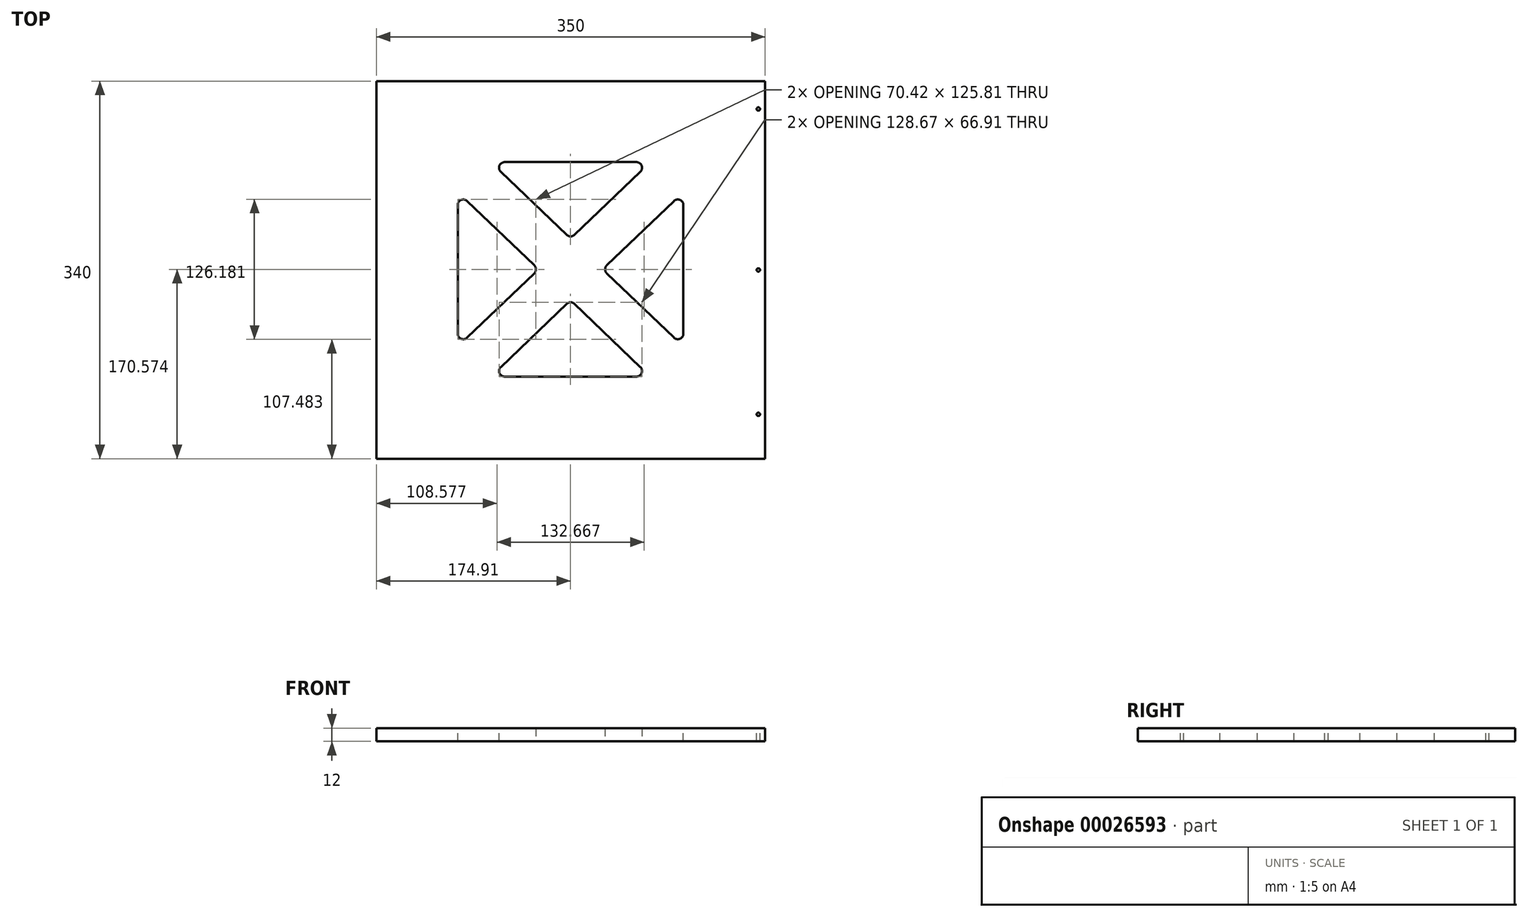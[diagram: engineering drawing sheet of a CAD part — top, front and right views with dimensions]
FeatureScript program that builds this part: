
annotation { "Feature Type Name" : "Feature", "Feature Type Description" : "" }
export const myFeature = defineFeature(function(context is Context, id is Id, definition is map)
    precondition{}
    {
        {
            var Q0;
            Q0=qCreatedBy(makeId("Top.planeOp"),FACE);
            var sketch = newSketch(context, id + "F0", { "sketchPlane" : qUnion([Q0])});
            skLineSegment(sketch, "E0.bottom", {"start": v(-70.96, 65.05) * mm, "end": v(279.04, 65.05) * mm});
            skLineSegment(sketch, "E0.top", {"start": v(-70.96, -274.95) * mm, "end": v(279.04, -274.95) * mm});
            skLineSegment(sketch, "E0.left", {"start": v(-70.96, 65.05) * mm, "end": v(-70.96, -274.95) * mm});
            skLineSegment(sketch, "E0.right", {"start": v(279.04, 65.05) * mm, "end": v(279.04, -274.95) * mm});
            skSolve(sketch);
        }
        {
            var Q0;
            Q0=qSketchRegion(id+"F0",true);
            extrude(context, id + "F1", {"entities" : qUnion([Q0]), "depth" : 12 * mm});
        }
        {
            var Q0;
            Q0=makeQuery(id+"F1.opExtrude","CAP_FACE",FACE,{"disambiguationData":[OSD([sQuery(id+"F0.wireOp",EDGE,"E0.bottom"),sQuery(id+"F0.wireOp",EDGE,"E0.top"),sQuery(id+"F0.wireOp",EDGE,"E0.left"),sQuery(id+"F0.wireOp",EDGE,"E0.right")])],"isStart":false});
            var sketch = newSketch(context, id + "F2", { "sketchPlane" : qUnion([Q0])});
            skLineSegment(sketch, "E1.0", {"start": v(2.4, -34.72) * mm, "end": v(75.05, -104.38) * mm});
            skLineSegment(sketch, "E2.trimOffspring", {"start": v(32.16, -7.83) * mm, "end": v(175.74, -7.83) * mm});
            skLineSegment(sketch, "E3.trimOffspring", {"start": v(103.95, -132.08) * mm, "end": v(175.74, -200.92) * mm});
            skLineSegment(sketch, "E4.2", {"start": v(175.74, -7.83) * mm, "end": v(103.95, -76.67) * mm});
            skLineSegment(sketch, "E5.1", {"start": v(32.16, -7.83) * mm, "end": v(103.95, -76.67) * mm});
            skLineSegment(sketch, "E6.trimOffspring", {"start": v(103.95, -132.08) * mm, "end": v(32.16, -200.92) * mm});
            skLineSegment(sketch, "E7.0", {"start": v(205.5, -34.72) * mm, "end": v(132.85, -104.38) * mm});
            skLineSegment(sketch, "E8.trimOffspring", {"start": v(75.05, -104.38) * mm, "end": v(2.4, -174.04) * mm});
            skLineSegment(sketch, "E9.trimOffspring", {"start": v(132.85, -104.38) * mm, "end": v(205.5, -174.04) * mm});
            skLineSegment(sketch, "E1.1", {"start": v(2.4, -34.72) * mm, "end": v(2.4, -174.04) * mm});
            skLineSegment(sketch, "E7.2", {"start": v(32.16, -200.92) * mm, "end": v(175.74, -200.92) * mm});
            skSolve(sketch);
        }
        {
            var Q0;
            Q0=qSketchRegion(id+"F2",true);
            extrude(context, id + "F3", {"entities" : qUnion([Q0]), "operationType" : NewBodyOperationType.REMOVE, "endBound" : BoundingType.THROUGH_ALL, "oppositeDirection" : true, "depth" : 25 * mm});
        }
        {
            var Q0;
            Q0=makeQuery(id+"F3.boolean.opBoolean","COPY",EDGE,{"derivedFrom":makeQuery(id+"F3.opExtrude","SWEPT_EDGE",EDGE,{"disambiguationData":[OSD([sQuery(id+"F2.wireOp",EDGE,"E1.0"),sQuery(id+"F2.wireOp",EDGE,"E1.1")])]})});
            var Q1;
            Q1=makeQuery(id+"F3.boolean.opBoolean","COPY",EDGE,{"derivedFrom":makeQuery(id+"F3.opExtrude","SWEPT_EDGE",EDGE,{"disambiguationData":[OSD([sQuery(id+"F2.wireOp",EDGE,"E8.trimOffspring"),sQuery(id+"F2.wireOp",EDGE,"E1.1")])]})});
            var Q2;
            Q2=makeQuery(id+"F3.boolean.opBoolean","COPY",EDGE,{"derivedFrom":makeQuery(id+"F3.opExtrude","SWEPT_EDGE",EDGE,{"disambiguationData":[OSD([sQuery(id+"F2.wireOp",EDGE,"E1.0"),sQuery(id+"F2.wireOp",EDGE,"E8.trimOffspring")])]})});
            var Q3;
            Q3=makeQuery(id+"F3.boolean.opBoolean","COPY",EDGE,{"derivedFrom":makeQuery(id+"F3.opExtrude","SWEPT_EDGE",EDGE,{"disambiguationData":[OSD([sQuery(id+"F2.wireOp",EDGE,"E6.trimOffspring"),sQuery(id+"F2.wireOp",EDGE,"E7.2")])]})});
            var Q4;
            Q4=makeQuery(id+"F3.boolean.opBoolean","COPY",EDGE,{"derivedFrom":makeQuery(id+"F3.opExtrude","SWEPT_EDGE",EDGE,{"disambiguationData":[OSD([sQuery(id+"F2.wireOp",EDGE,"E3.trimOffspring"),sQuery(id+"F2.wireOp",EDGE,"E6.trimOffspring")])]})});
            var Q5;
            Q5=makeQuery(id+"F3.boolean.opBoolean","COPY",EDGE,{"derivedFrom":makeQuery(id+"F3.opExtrude","SWEPT_EDGE",EDGE,{"disambiguationData":[OSD([sQuery(id+"F2.wireOp",EDGE,"E3.trimOffspring"),sQuery(id+"F2.wireOp",EDGE,"E7.2")])]})});
            var Q6;
            Q6=makeQuery(id+"F3.boolean.opBoolean","COPY",EDGE,{"derivedFrom":makeQuery(id+"F3.opExtrude","SWEPT_EDGE",EDGE,{"disambiguationData":[OSD([sQuery(id+"F2.wireOp",EDGE,"E7.0"),sQuery(id+"F2.wireOp",EDGE,"E9.trimOffspring")])]})});
            var Q7;
            Q7=makeQuery(id+"F3.boolean.opBoolean","COPY",EDGE,{"derivedFrom":makeQuery(id+"F3.opExtrude","SWEPT_EDGE",EDGE,{"disambiguationData":[OSD([sQuery(id+"F2.wireOp",EDGE,"E9.trimOffspring"),sQuery(id+"F2.wireOp",EDGE,"E5.2")])]})});
            var Q8;
            Q8=makeQuery(id+"F3.boolean.opBoolean","COPY",EDGE,{"derivedFrom":makeQuery(id+"F3.opExtrude","SWEPT_EDGE",EDGE,{"disambiguationData":[OSD([sQuery(id+"F2.wireOp",EDGE,"E7.0"),sQuery(id+"F2.wireOp",EDGE,"E5.2")])]})});
            var Q9;
            Q9=makeQuery(id+"F3.boolean.opBoolean","COPY",EDGE,{"derivedFrom":makeQuery(id+"F3.opExtrude","SWEPT_EDGE",EDGE,{"disambiguationData":[OSD([sQuery(id+"F2.wireOp",EDGE,"E4.2"),sQuery(id+"F2.wireOp",EDGE,"E2.trimOffspring")])]})});
            var Q10;
            Q10=makeQuery(id+"F3.boolean.opBoolean","COPY",EDGE,{"derivedFrom":makeQuery(id+"F3.opExtrude","SWEPT_EDGE",EDGE,{"disambiguationData":[OSD([sQuery(id+"F2.wireOp",EDGE,"E4.2"),sQuery(id+"F2.wireOp",EDGE,"E5.1")])]})});
            var Q11;
            Q11=makeQuery(id+"F3.boolean.opBoolean","COPY",EDGE,{"derivedFrom":makeQuery(id+"F3.opExtrude","SWEPT_EDGE",EDGE,{"disambiguationData":[OSD([sQuery(id+"F2.wireOp",EDGE,"E5.1"),sQuery(id+"F2.wireOp",EDGE,"E2.trimOffspring")])]})});
            fillet(context, id + "F4", {"entities" : qUnion([Q0, Q1, Q2, Q3, Q4, Q5, Q6, Q7, Q8, Q9, Q10, Q11]), "radius" : 5 * mm, "tangentPropagation" : true, "allowEdgeOverflow" : false});
        }
        {
            var Q0;
            Q0=makeQuery(id+"F1.opExtrude","CAP_FACE",FACE,{"disambiguationData":[OSD([sQuery(id+"F0.wireOp",EDGE,"E0.bottom"),sQuery(id+"F0.wireOp",EDGE,"E0.top"),sQuery(id+"F0.wireOp",EDGE,"E0.left"),sQuery(id+"F0.wireOp",EDGE,"E0.right")])],"isStart":false});
            var sketch = newSketch(context, id + "F5", { "sketchPlane" : qUnion([Q0])});
            skCircle(sketch, "E10", {"center": v(273.04, -104.95) * mm, "radius": 1.5 * mm});
            skCircle(sketch, "E11", {"center": v(273.04, 40.05) * mm, "radius": 1.5 * mm});
            skCircle(sketch, "E12", {"center": v(273.04, -234.95) * mm, "radius": 1.5 * mm});
            skLineSegment(sketch, "E13", {"start": v(104.04, -274.95) * mm, "end": v(104.04, -86.13) * mm, "construction": true});
            skLineSegment(sketch, "E14", {"start": v(279.04, -104.95) * mm, "end": v(104.04, -104.95) * mm, "construction": true});
            skSolve(sketch);
        }
        {
            var Q0;
            Q0=qSketchRegion(id+"F5",true);
            extrude(context, id + "F6", {"entities" : qUnion([Q0]), "operationType" : NewBodyOperationType.REMOVE, "endBound" : BoundingType.THROUGH_ALL, "oppositeDirection" : true, "depth" : 25 * mm});
        }
    });
